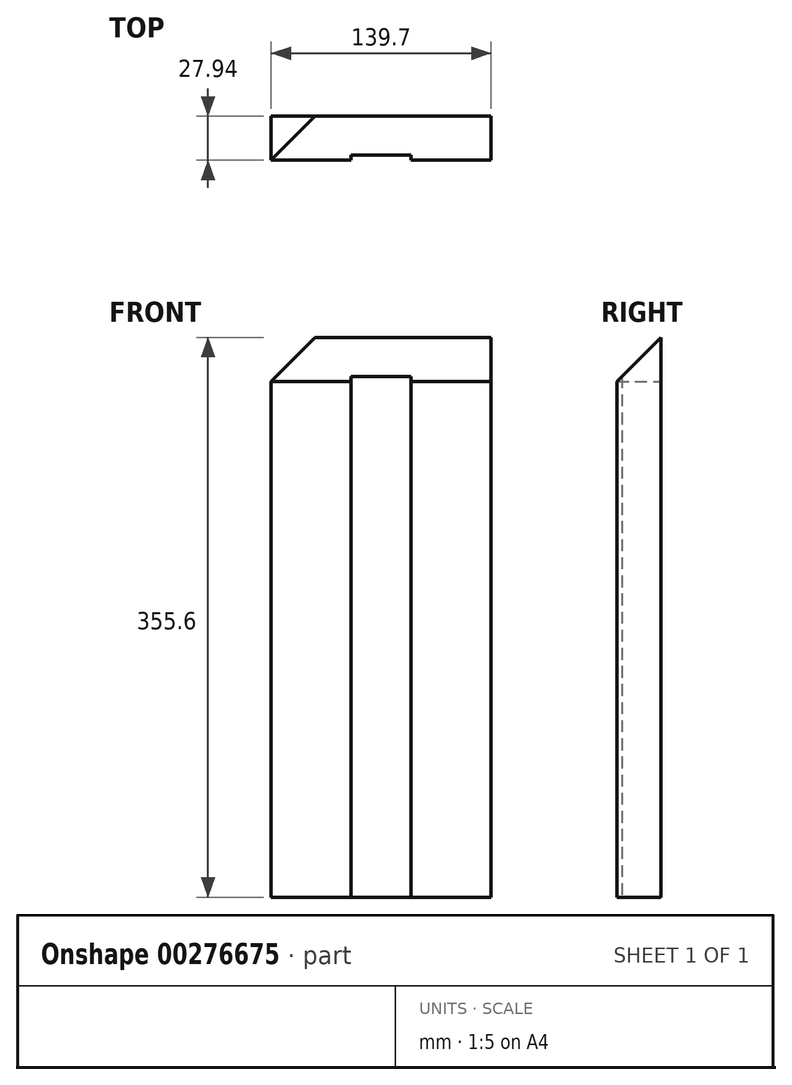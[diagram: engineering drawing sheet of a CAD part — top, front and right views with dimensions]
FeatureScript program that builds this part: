
annotation { "Feature Type Name" : "Feature", "Feature Type Description" : "" }
export const myFeature = defineFeature(function(context is Context, id is Id, definition is map)
    precondition{}
    {
        {
            var Q0;
            Q0=qCreatedBy(makeId("Top.planeOp"),FACE);
            var sketch = newSketch(context, id + "F0", { "sketchPlane" : qUnion([Q0])});
            skLineSegment(sketch, "E0.bottom", {"start": v(0, 0) * mm, "end": v(139.7, 0) * mm});
            skLineSegment(sketch, "E0.top", {"start": v(0, -27.94) * mm, "end": v(139.7, -27.94) * mm});
            skLineSegment(sketch, "E0.left", {"start": v(0, -27.94) * mm, "end": v(0, 0) * mm});
            skLineSegment(sketch, "E0.right", {"start": v(139.7, -27.94) * mm, "end": v(139.7, 0) * mm});
            skSolve(sketch);
        }
        {
            var Q0;
            Q0=qSketchRegion(id+"F0",true);
            extrude(context, id + "F1", {"entities" : qUnion([Q0]), "depth" : 355.6 * mm});
        }
        {
            var Q0;
            Q0=makeQuery(id+"F1.opExtrude","CAP_EDGE",EDGE,{"disambiguationData":[OSD([sQuery(id+"F0.wireOp",EDGE,"E0.top")])],"isStart":false});
            chamfer(context, id + "F2", {"entities" : qUnion([Q0]), "width" : 27.94 * mm, "tangentPropagation" : true});
        }
        {
            var Q0;
            Q0=makeQuery(id+"F1.opExtrude","SWEPT_FACE",FACE,{"disambiguationData":[OSD([sQuery(id+"F0.wireOp",EDGE,"E0.top")])]});
            var sketch = newSketch(context, id + "F3", { "sketchPlane" : qUnion([Q0])});
            skLineSegment(sketch, "E1.bottom", {"start": v(50.8, 355.6) * mm, "end": v(88.9, 355.6) * mm});
            skLineSegment(sketch, "E1.top", {"start": v(50.8, 0) * mm, "end": v(88.9, 0) * mm});
            skLineSegment(sketch, "E1.left", {"start": v(50.8, 355.6) * mm, "end": v(50.8, 0) * mm});
            skLineSegment(sketch, "E1.right", {"start": v(88.9, 355.6) * mm, "end": v(88.9, 0) * mm});
            skSolve(sketch);
        }
        {
            var Q0;
            Q0=qSketchRegion(id+"F3",true);
            extrude(context, id + "F4", {"entities" : qUnion([Q0]), "operationType" : NewBodyOperationType.REMOVE, "oppositeDirection" : true, "depth" : 3.17 * mm});
        }
        {
            var Q0;
            Q0=makeQuery(id+"F1.opExtrude","SWEPT_FACE",FACE,{"disambiguationData":[OSD([sQuery(id+"F0.wireOp",EDGE,"E0.bottom")])]});
            var sketch = newSketch(context, id + "F5", { "sketchPlane" : qUnion([Q0])});
            skLineSegment(sketch, "E2", {"start": v(0, 355.6) * mm, "end": v(-27.94, 355.6) * mm});
            skLineSegment(sketch, "E3", {"start": v(-27.94, 355.6) * mm, "end": v(0, 327.66) * mm});
            skLineSegment(sketch, "E4", {"start": v(0, 327.66) * mm, "end": v(0, 355.6) * mm});
            skSolve(sketch);
        }
        {
            var Q0;
            Q0=makeQuery(id+"F5.imprint","IMPRINT",FACE,{"disambiguationData":[TD([[makeQuery(id+"F5.imprint","IMPRINT",EDGE,{"derivedFrom":sQuery(id+"F5.wireOp",EDGE,"E2")}),1.0]])]});
            extrude(context, id + "F6", {"entities" : qUnion([Q0]), "operationType" : NewBodyOperationType.REMOVE, "oppositeDirection" : true, "depth" : 38.1 * mm});
        }
    });
